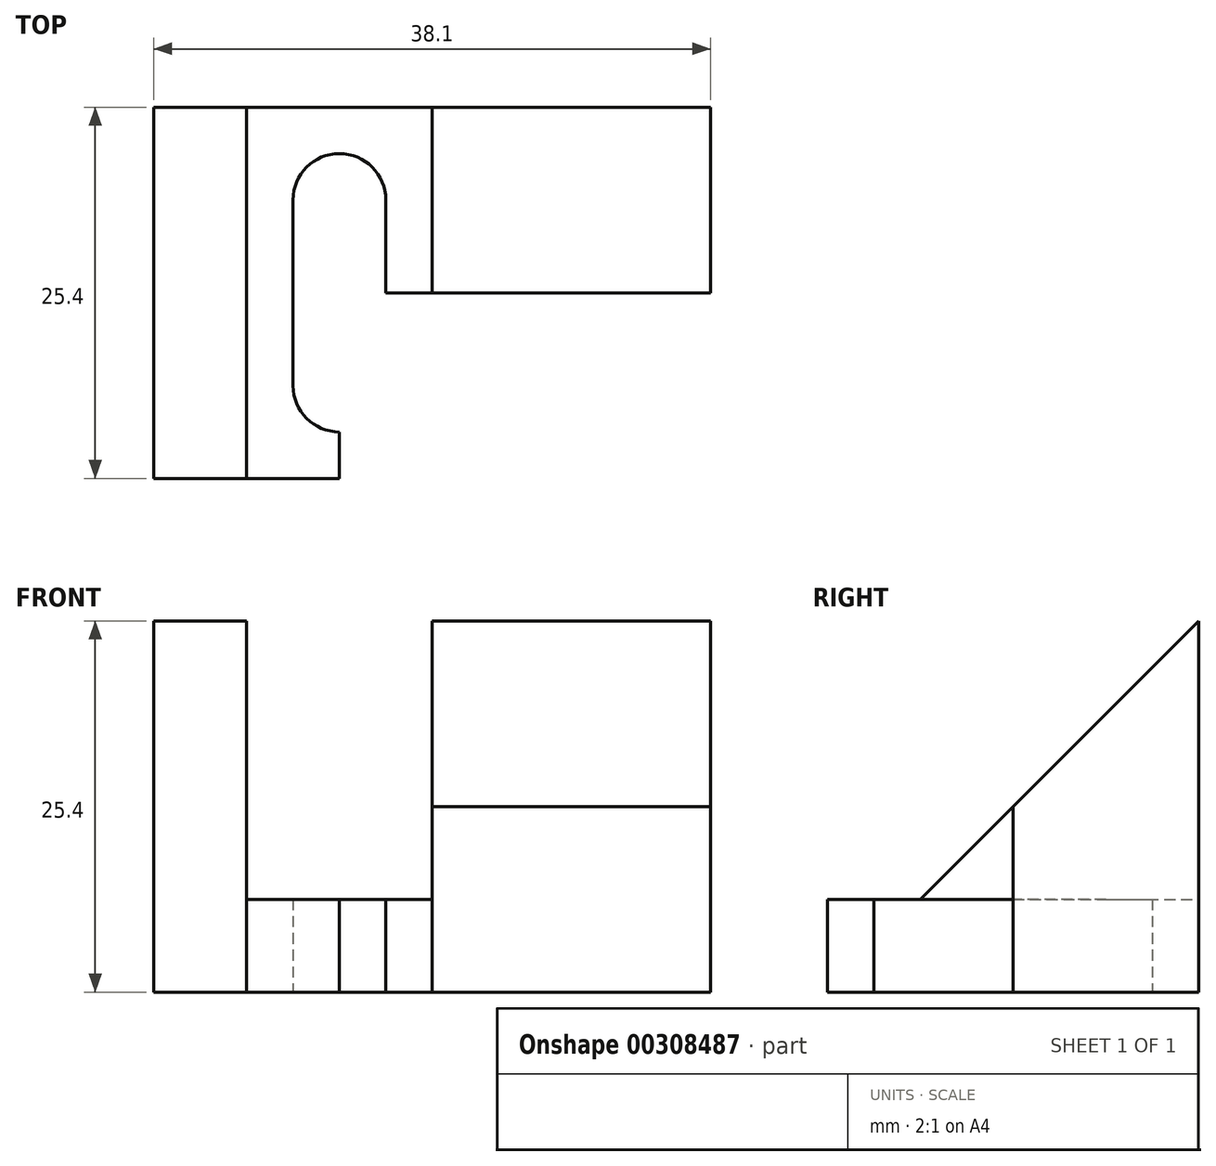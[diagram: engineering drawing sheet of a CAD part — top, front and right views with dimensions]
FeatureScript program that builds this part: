
annotation { "Feature Type Name" : "Feature", "Feature Type Description" : "" }
export const myFeature = defineFeature(function(context is Context, id is Id, definition is map)
    precondition{}
    {
        {
            var Q0;
            Q0=qCreatedBy(makeId("Top.planeOp"),FACE);
            var sketch = newSketch(context, id + "F0", { "sketchPlane" : qUnion([Q0])});
            skLineSegment(sketch, "E0", {"start": v(-35.8, 27.72) * mm, "end": v(-35.8, 2.32) * mm});
            skLineSegment(sketch, "E1", {"start": v(-35.8, 2.32) * mm, "end": v(-29.46, 2.32) * mm});
            skLineSegment(sketch, "E2", {"start": v(-29.46, 2.32) * mm, "end": v(-29.46, 27.72) * mm});
            skLineSegment(sketch, "E3", {"start": v(-29.46, 27.72) * mm, "end": v(-35.8, 27.72) * mm});
            skSolve(sketch);
        }
        {
            var Q0;
            Q0 = qSketchRegion(id + "F0", true);
            extrude(context, id + "F1", {"entities" : qUnion([Q0]), "depth" : 25.4 * mm});
        }
        {
            var Q0;
            Q0=makeQuery(id+"F1.opExtrude","CAP_FACE",FACE,{"disambiguationData":[OSD([sQuery(id+"F0.wireOp",EDGE,"E0"),sQuery(id+"F0.wireOp",EDGE,"E1"),sQuery(id+"F0.wireOp",EDGE,"E2"),sQuery(id+"F0.wireOp",EDGE,"E3")])],"isStart":true});
            var sketch = newSketch(context, id + "F2", { "sketchPlane" : qUnion([Q0])});
            skLineSegment(sketch, "E4", {"start": v(-29.46, -2.32) * mm, "end": v(-16.76, -2.32) * mm});
            skLineSegment(sketch, "E5", {"start": v(-16.76, -2.32) * mm, "end": v(-16.76, -27.72) * mm});
            skLineSegment(sketch, "E6", {"start": v(-16.76, -27.72) * mm, "end": v(-29.46, -27.72) * mm});
            skLineSegment(sketch, "E7", {"start": v(-29.46, -27.72) * mm, "end": v(-29.46, -2.32) * mm});
            skCircle(sketch, "E8", {"center": v(-23.1, -21.37) * mm, "radius": 3.18 * mm});
            skPoint(sketch, "E8.centerSnap0", {"position": v(-23.1, -27.72) * mm});
            skCircle(sketch, "E9", {"center": v(-23.1, -8.67) * mm, "radius": 3.18 * mm});
            skPoint(sketch, "E9.centerSnap0", {"position": v(-23.1, -2.32) * mm});
            skLineSegment(sketch, "E10", {"start": v(-26.28, -21.37) * mm, "end": v(-26.28, -8.67) * mm});
            skLineSegment(sketch, "E11", {"start": v(-19.93, -8.67) * mm, "end": v(-19.93, -21.37) * mm});
            skSolve(sketch);
        }
        {
            var Q0;
            Q0 = qSketchRegion(id + "F2", true);
            extrude(context, id + "F3", {"entities" : qUnion([Q0]), "oppositeDirection" : true, "depth" : 6.35 * mm});
        }
        {
            var Q0;
            Q0=makeQuery(id+"F3.opExtrude","CAP_FACE",FACE,{"disambiguationData":[OSD([sQuery(id+"F2.wireOp",EDGE,"E4"),sQuery(id+"F2.wireOp",EDGE,"E5"),sQuery(id+"F2.wireOp",EDGE,"E6"),sQuery(id+"F2.wireOp",EDGE,"E7"),sQuery(id+"F2.wireOp",EDGE,"E8"),sQuery(id+"F2.wireOp",EDGE,"E9")])],"isStart":true});
            var sketch = newSketch(context, id + "F4", { "sketchPlane" : qUnion([Q0])});
            skLineSegment(sketch, "E12", {"start": v(-16.76, -2.32) * mm, "end": v(2.3, -2.32) * mm});
            skLineSegment(sketch, "E13", {"start": v(2.3, -2.32) * mm, "end": v(2.3, -27.72) * mm});
            skLineSegment(sketch, "E14", {"start": v(2.3, -27.72) * mm, "end": v(-16.76, -27.72) * mm});
            skLineSegment(sketch, "E15", {"start": v(-16.76, -27.72) * mm, "end": v(-16.76, -2.32) * mm});
            skSolve(sketch);
        }
        {
            var Q0;
            Q0 = qSketchRegion(id + "F4", true);
            extrude(context, id + "F5", {"entities" : qUnion([Q0]), "oppositeDirection" : true, "depth" : 12.7 * mm});
        }
        {
            var Q0;
            Q0=makeQuery(id+"F5.opExtrude","SWEPT_FACE",FACE,{"disambiguationData":[OSD([sQuery(id+"F4.wireOp",EDGE,"E13")])]});
            var sketch = newSketch(context, id + "F6", { "sketchPlane" : qUnion([Q0])});
            skLineSegment(sketch, "E16", {"start": v(2.32, 0) * mm, "end": v(15.02, 0) * mm});
            skLineSegment(sketch, "E17", {"start": v(15.02, 0) * mm, "end": v(15.02, 12.7) * mm});
            skLineSegment(sketch, "E18", {"start": v(15.02, 12.7) * mm, "end": v(2.32, 12.7) * mm});
            skLineSegment(sketch, "E19", {"start": v(2.32, 12.7) * mm, "end": v(2.32, 0) * mm});
            skSolve(sketch);
        }
        {
            var Q0;
            Q0 = qSketchRegion(id + "F6", true);
            extrude(context, id + "F7", {"entities" : qUnion([Q0]), "operationType" : NewBodyOperationType.REMOVE, "oppositeDirection" : true, "depth" : 25.4 * mm});
        }
        {
            var Q0;
            Q0=makeQuery(id+"F1.opExtrude","SWEPT_FACE",FACE,{"disambiguationData":[OSD([sQuery(id+"F0.wireOp",EDGE,"E0")])]});
            var sketch = newSketch(context, id + "F8", { "sketchPlane" : qUnion([Q0])});
            skLineSegment(sketch, "E20", {"start": v(-2.32, 0) * mm, "end": v(-27.72, 25.4) * mm});
            skLineSegment(sketch, "E21", {"start": v(-27.72, 25.4) * mm, "end": v(-2.32, 25.4) * mm});
            skLineSegment(sketch, "E22", {"start": v(-2.32, 25.4) * mm, "end": v(-2.32, 0) * mm});
            skSolve(sketch);
        }
        {
            var Q0;
            Q0 = qSketchRegion(id + "F8", true);
            extrude(context, id + "F9", {"entities" : qUnion([Q0]), "operationType" : NewBodyOperationType.REMOVE, "oppositeDirection" : true, "depth" : 6.35 * mm});
        }
        {
            var Q0;
            Q0=makeQuery(id+"F5.opExtrude","SWEPT_FACE",FACE,{"disambiguationData":[OSD([sQuery(id+"F4.wireOp",EDGE,"E13")])]});
            var sketch = newSketch(context, id + "F10", { "sketchPlane" : qUnion([Q0])});
            skLineSegment(sketch, "E23", {"start": v(15.02, 12.7) * mm, "end": v(27.72, 12.7) * mm});
            skLineSegment(sketch, "E24", {"start": v(27.72, 12.7) * mm, "end": v(27.72, 25.4) * mm});
            skLineSegment(sketch, "E25", {"start": v(27.72, 25.4) * mm, "end": v(15.02, 12.7) * mm});
            skSolve(sketch);
        }
        {
            var Q0;
            Q0 = qSketchRegion(id + "F10", true);
            extrude(context, id + "F11", {"entities" : qUnion([Q0]), "operationType" : NewBodyOperationType.ADD, "oppositeDirection" : true, "depth" : 19.05 * mm});
        }
    });
